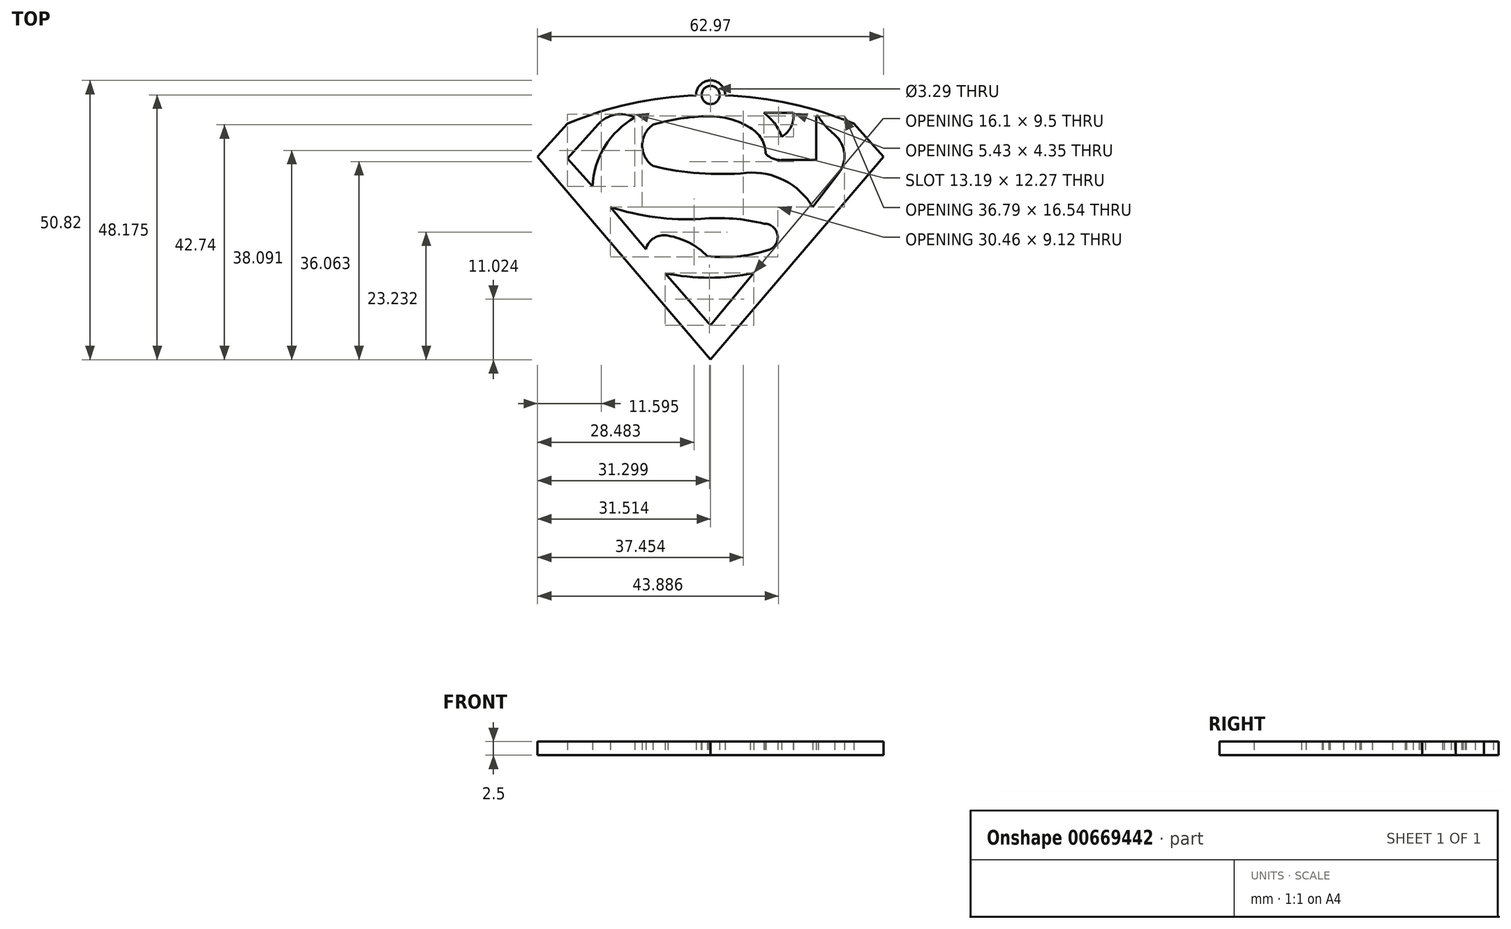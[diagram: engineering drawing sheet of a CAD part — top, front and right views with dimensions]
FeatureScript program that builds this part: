
annotation { "Feature Type Name" : "Feature", "Feature Type Description" : "" }
export const myFeature = defineFeature(function(context is Context, id is Id, definition is map)
    precondition{}
    {
        {
            var Q0;
            Q0=qCreatedBy(makeId("Top.planeOp"),FACE);
            var sketch = newSketch(context, id + "F0", { "sketchPlane" : qUnion([Q0])});
            skLineSegment(sketch, "E0", {"start": v(100, 0) * mm, "end": v(-100, 0) * mm, "construction": true});
            skLineSegment(sketch, "E1", {"start": v(0, 100) * mm, "end": v(0, -100) * mm, "construction": true});
            skLineSegment(sketch, "E2", {"start": v(24.59, 16.56) * mm, "end": v(32.82, 7.1) * mm});
            skLineSegment(sketch, "E3", {"start": v(32.82, 7.1) * mm, "end": v(40.69, 16.6) * mm});
            skArc(sketch, "E4", {"start": v(24.59, 16.56) * mm, "mid": v(32.64, 15.74) * mm, "end": v(40.69, 16.6) * mm});
            skLineSegment(sketch, "E5", {"start": v(47.89, 45.74) * mm, "end": v(42.5, 45.74) * mm});
            skArc(sketch, "E6", {"start": v(45.76, 41.38) * mm, "mid": v(44.5, 43.83) * mm, "end": v(42.5, 45.74) * mm});
            skArc(sketch, "E7", {"start": v(45.76, 41.38) * mm, "mid": v(47.51, 43.22) * mm, "end": v(47.89, 45.74) * mm});
            skArc(sketch, "E8", {"start": v(42.88, 38.3) * mm, "mid": v(44.2, 37.4) * mm, "end": v(45.76, 37.14) * mm});
            skArc(sketch, "E9", {"start": v(42.88, 38.3) * mm, "mid": v(42.1, 41.02) * mm, "end": v(40.08, 43) * mm});
            skArc(sketch, "E10", {"start": v(40.08, 43) * mm, "mid": v(36.42, 44.61) * mm, "end": v(32.45, 45.1) * mm});
            skArc(sketch, "E11", {"start": v(32.45, 45.1) * mm, "mid": v(27.35, 44.72) * mm, "end": v(22.35, 43.58) * mm});
            skArc(sketch, "E12", {"start": v(22.35, 43.58) * mm, "mid": v(20.4, 39.82) * mm, "end": v(22.35, 36.07) * mm});
            skArc(sketch, "E13", {"start": v(22.35, 36.07) * mm, "mid": v(30.8, 34.74) * mm, "end": v(39.33, 34.8) * mm});
            skArc(sketch, "E14", {"start": v(51.43, 28.62) * mm, "mid": v(46.28, 33.46) * mm, "end": v(39.33, 34.8) * mm});
            skLineSegment(sketch, "E15", {"start": v(51.43, 28.62) * mm, "end": v(56.16, 34.8) * mm});
            skArc(sketch, "E16", {"start": v(56.16, 34.8) * mm, "mid": v(57.18, 38.4) * mm, "end": v(55.46, 41.73) * mm});
            skArc(sketch, "E17", {"start": v(52.42, 45.15) * mm, "mid": v(53.79, 43.3) * mm, "end": v(55.46, 41.73) * mm});
            skLineSegment(sketch, "E18", {"start": v(52.04, 45.15) * mm, "end": v(52.04, 37.14) * mm});
            skLineSegment(sketch, "E19", {"start": v(52.04, 37.14) * mm, "end": v(45.76, 37.14) * mm});
            skLineSegment(sketch, "E20", {"start": v(12.36, 43.63) * mm, "end": v(6.8, 37.43) * mm});
            skLineSegment(sketch, "E21", {"start": v(6.8, 37.43) * mm, "end": v(11.34, 32.32) * mm});
            skArc(sketch, "E22", {"start": v(19.07, 44.91) * mm, "mid": v(13.58, 39.62) * mm, "end": v(11.34, 32.32) * mm});
            skArc(sketch, "E23", {"start": v(19.07, 44.91) * mm, "mid": v(15.5, 45.4) * mm, "end": v(12.36, 43.63) * mm});
            skLineSegment(sketch, "E24", {"start": v(14.6, 28.61) * mm, "end": v(21.05, 20.94) * mm});
            skArc(sketch, "E25", {"start": v(25.08, 23.37) * mm, "mid": v(22.57, 22.97) * mm, "end": v(21.05, 20.94) * mm});
            skArc(sketch, "E26", {"start": v(32.24, 19.66) * mm, "mid": v(28.96, 22.1) * mm, "end": v(25.08, 23.37) * mm});
            skArc(sketch, "E27", {"start": v(42.93, 20.67) * mm, "mid": v(45.05, 23.28) * mm, "end": v(42.59, 25.57) * mm});
            skArc(sketch, "E28", {"start": v(32.24, 19.66) * mm, "mid": v(37.64, 19.6) * mm, "end": v(42.93, 20.67) * mm});
            skArc(sketch, "E29", {"start": v(42.59, 25.57) * mm, "mid": v(36.88, 26.49) * mm, "end": v(31.1, 26.44) * mm});
            skArc(sketch, "E30", {"start": v(14.6, 28.61) * mm, "mid": v(22.75, 26.76) * mm, "end": v(31.1, 26.44) * mm});
            skLineSegment(sketch, "E31", {"start": v(1.34, 37.72) * mm, "end": v(32.82, 0.82) * mm});
            skLineSegment(sketch, "E32", {"start": v(32.82, 0.82) * mm, "end": v(64.31, 37.72) * mm});
            skLineSegment(sketch, "E33", {"start": v(64.31, 37.72) * mm, "end": v(58.93, 43.78) * mm});
            skLineSegment(sketch, "E34", {"start": v(1.34, 37.72) * mm, "end": v(6.78, 43.78) * mm});
            skArc(sketch, "E35", {"start": v(58.93, 43.78) * mm, "mid": v(47.44, 47.4) * mm, "end": v(35.5, 48.94) * mm});
            skLineSegment(sketch, "E36", {"start": v(52.04, 45.15) * mm, "end": v(52.42, 45.15) * mm});
            skArc(sketch, "E37", {"start": v(35.5, 48.94) * mm, "mid": v(32.85, 51.64) * mm, "end": v(30.2, 48.94) * mm});
            skCircle(sketch, "E38", {"center": v(32.85, 49) * mm, "radius": 1.65 * mm});
            skArc(sketch, "E39.trimOffspring", {"start": v(30.2, 48.94) * mm, "mid": v(18.26, 47.4) * mm, "end": v(6.78, 43.78) * mm});
            skSolve(sketch);
        }
        {
            var Q0;
            Q0=makeQuery(id+"F0.imprint","IMPRINT",FACE,{"disambiguationData":[TD([[makeQuery(id+"F0.imprint","IMPRINT",EDGE,{"derivedFrom":sQuery(id+"F0.wireOp",EDGE,"E2")}),-1.0]])]});
            extrude(context, id + "F1", {"entities" : qUnion([Q0]), "depth" : 2.5 * mm, "offsetDistance" : 25 * mm});
        }
    });
